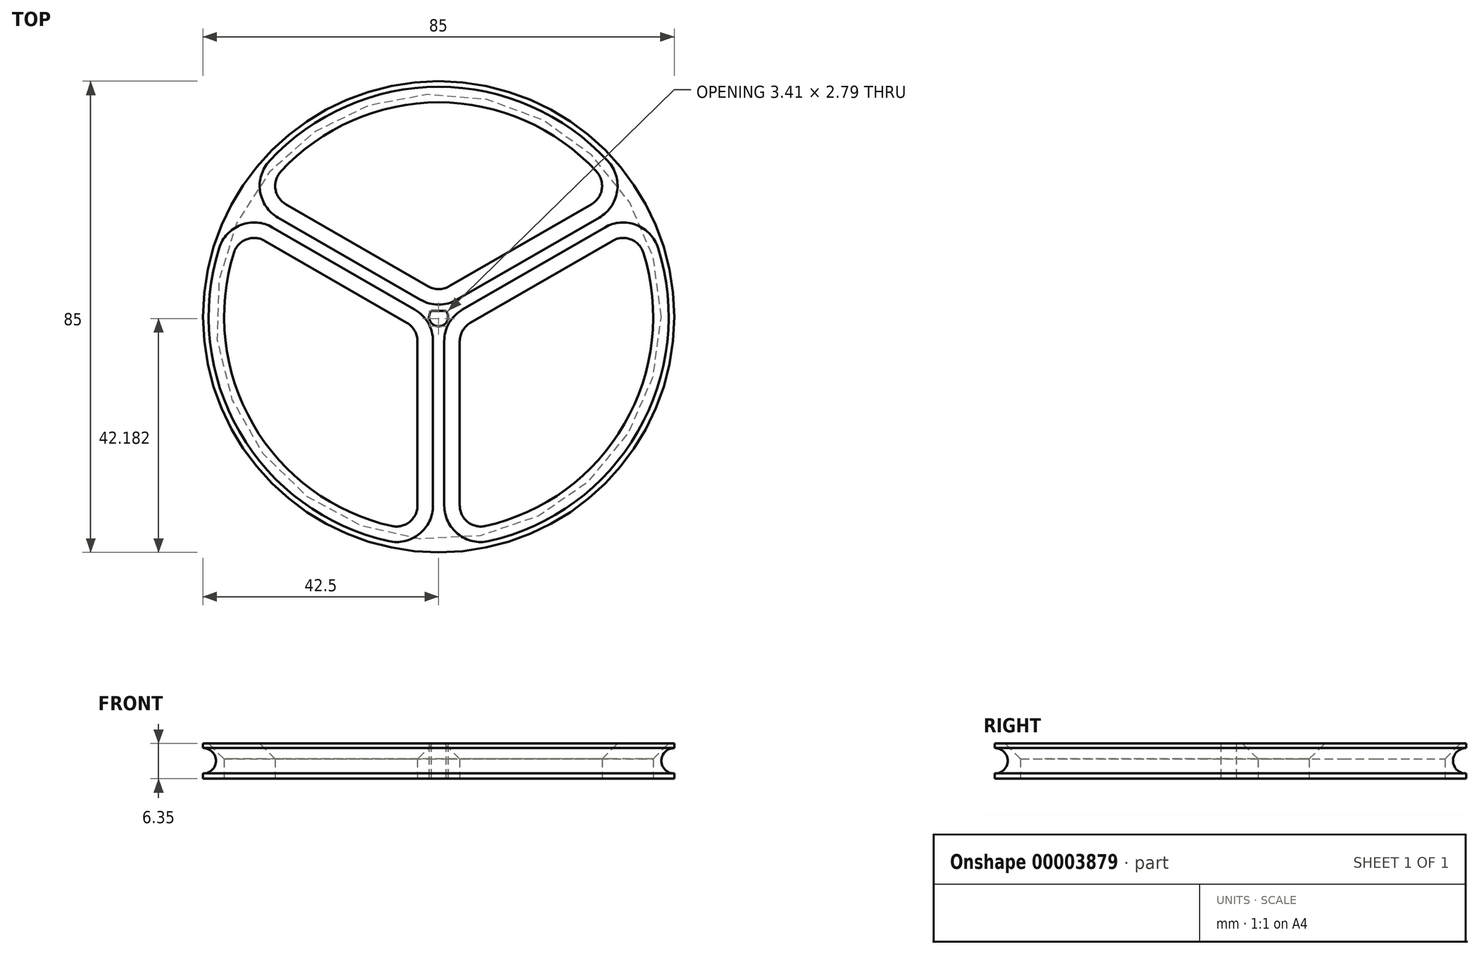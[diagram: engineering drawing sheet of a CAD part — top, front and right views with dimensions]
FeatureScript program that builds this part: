
annotation { "Feature Type Name" : "Feature", "Feature Type Description" : "" }
export const myFeature = defineFeature(function(context is Context, id is Id, definition is map)
    precondition{}
    {
        {
            var Q0;
            Q0=qCreatedBy(makeId("Top.planeOp"),FACE);
            var sketch = newSketch(context, id + "F0", { "sketchPlane" : qUnion([Q0])});
            skCircle(sketch, "E0", {"center": v(0, 0) * mm, "radius": 42.5 * mm});
            skLineSegment(sketch, "E1", {"start": v(0, 0) * mm, "end": v(-36.8, 21.25) * mm});
            skLineSegment(sketch, "E2", {"start": v(0, 0) * mm, "end": v(36.8, 21.25) * mm});
            skLineSegment(sketch, "E3", {"start": v(0, 0) * mm, "end": v(-36.8, -21.25) * mm, "construction": true});
            skLineSegment(sketch, "E4", {"start": v(0, 0) * mm, "end": v(0, -42.5) * mm});
            skLineSegment(sketch, "E5", {"start": v(0, 0) * mm, "end": v(36.8, -21.25) * mm, "construction": true});
            skLineSegment(sketch, "E6", {"start": v(0, 0) * mm, "end": v(0, 42.5) * mm, "construction": true});
            skArc(sketch, "E7", {"start": v(-1.33, 1.08) * mm, "mid": v(0, -1.71) * mm, "end": v(1.33, 1.08) * mm});
            skPoint(sketch, "E8", {"position": v(0, 1.08) * mm});
            skLineSegment(sketch, "E9", {"start": v(0, 1.08) * mm, "end": v(1.33, 1.08) * mm});
            skLineSegment(sketch, "E10", {"start": v(0, 1.08) * mm, "end": v(-1.33, 1.08) * mm});
            skLineSegment(sketch, "E11.0", {"start": v(5.71, -1.1) * mm, "end": v(31.38, 13.72) * mm});
            skLineSegment(sketch, "E11.1", {"start": v(3.81, -4.4) * mm, "end": v(3.81, -34.04) * mm});
            skLineSegment(sketch, "E12.0", {"start": v(-5.71, -1.1) * mm, "end": v(-31.38, 13.72) * mm});
            skLineSegment(sketch, "E12.1", {"start": v(-3.81, -4.4) * mm, "end": v(-3.8, -34.04) * mm});
            skLineSegment(sketch, "E13.0", {"start": v(-1.9, 5.5) * mm, "end": v(-27.57, 20.32) * mm});
            skLineSegment(sketch, "E13.1", {"start": v(1.9, 5.5) * mm, "end": v(27.57, 20.32) * mm});
            skArc(sketch, "E14", {"start": v(-36.92, 11.56) * mm, "mid": v(-33.5, -19.35) * mm, "end": v(-8.45, -37.76) * mm});
            skArc(sketch, "E15", {"start": v(8.45, -37.76) * mm, "mid": v(33.5, -19.35) * mm, "end": v(36.92, 11.56) * mm});
            skArc(sketch, "E16", {"start": v(28.47, 26.2) * mm, "mid": v(0, 38.7) * mm, "end": v(-28.47, 26.2) * mm});
            skPoint(sketch, "E17.visualSharp", {"position": v(-31.44, 22.55) * mm});
            skArc(sketch, "E17.filletArc", {"start": v(-28.47, 26.2) * mm, "mid": v(-29.43, 23.04) * mm, "end": v(-27.57, 20.32) * mm});
            skPoint(sketch, "E18.visualSharp", {"position": v(31.44, 22.55) * mm});
            skArc(sketch, "E18.filletArc", {"start": v(27.57, 20.32) * mm, "mid": v(29.43, 23.04) * mm, "end": v(28.47, 26.2) * mm});
            skPoint(sketch, "E19.visualSharp", {"position": v(0, 4.4) * mm});
            skArc(sketch, "E19.filletArc", {"start": v(-1.9, 5.5) * mm, "mid": v(0, 4.99) * mm, "end": v(1.9, 5.5) * mm});
            skPoint(sketch, "E20.visualSharp", {"position": v(-3.8, -2.2) * mm});
            skArc(sketch, "E20.filletArc", {"start": v(-3.81, -4.4) * mm, "mid": v(-4.32, -2.5) * mm, "end": v(-5.71, -1.1) * mm});
            skPoint(sketch, "E21.visualSharp", {"position": v(-35.25, 15.95) * mm});
            skArc(sketch, "E21.filletArc", {"start": v(-31.38, 13.72) * mm, "mid": v(-34.67, 13.97) * mm, "end": v(-36.92, 11.56) * mm});
            skPoint(sketch, "E22.visualSharp", {"position": v(-3.8, -38.5) * mm});
            skArc(sketch, "E22.filletArc", {"start": v(-8.45, -37.76) * mm, "mid": v(-5.24, -37.01) * mm, "end": v(-3.8, -34.04) * mm});
            skPoint(sketch, "E23.visualSharp", {"position": v(3.81, -38.5) * mm});
            skArc(sketch, "E23.filletArc", {"start": v(3.81, -34.04) * mm, "mid": v(5.24, -37.01) * mm, "end": v(8.45, -37.76) * mm});
            skPoint(sketch, "E24.visualSharp", {"position": v(3.8, -2.2) * mm});
            skArc(sketch, "E24.filletArc", {"start": v(5.71, -1.1) * mm, "mid": v(4.32, -2.5) * mm, "end": v(3.8, -4.4) * mm});
            skPoint(sketch, "E25.visualSharp", {"position": v(35.25, 15.95) * mm});
            skArc(sketch, "E25.filletArc", {"start": v(36.92, 11.56) * mm, "mid": v(34.67, 13.97) * mm, "end": v(31.38, 13.72) * mm});
            skSolve(sketch);
        }
        {
            var Q0;
            {var subQ1=sQuery(id+"F0.wireOp",EDGE,"E9");Q0=qUnion([makeQuery(id+"F0.imprint","IMPRINT",FACE,{"disambiguationData":[TD([[makeQuery(id+"F0.imprint","IMPRINT",EDGE,{"derivedFrom":subQ1}),1.0]])]}),makeQuery(id+"F0.imprint","IMPRINT",FACE,{"disambiguationData":[TD([[makeQuery(id+"F0.imprint","IMPRINT",EDGE,{"derivedFrom":sQuery(id+"F0.wireOp",EDGE,"E12.0")}),-1.0]])]}),makeQuery(id+"F0.imprint","IMPRINT",FACE,{"disambiguationData":[TD([[makeQuery(id+"F0.imprint","IMPRINT",EDGE,{"derivedFrom":sQuery(id+"F0.wireOp",EDGE,"E11.0")}),1.0]])]})]);}
            extrude(context, id + "F1", {"entities" : qUnion([Q0]), "depth" : 6.35 * mm});
        }
        {
            var Q0;
            Q0=makeQuery(id+"F1.opExtrude","CAP_EDGE",EDGE,{"disambiguationData":[OSD([sQuery(id+"F0.wireOp",EDGE,"E16")])],"isStart":false});
            var Q1;
            Q1=makeQuery(id+"F1.opExtrude","CAP_EDGE",EDGE,{"disambiguationData":[OSD([sQuery(id+"F0.wireOp",EDGE,"E17.filletArc")])],"isStart":false});
            var Q2;
            Q2=makeQuery(id+"F1.opExtrude","CAP_EDGE",EDGE,{"disambiguationData":[OSD([sQuery(id+"F0.wireOp",EDGE,"E13.0")])],"isStart":false});
            var Q3;
            Q3=makeQuery(id+"F1.opExtrude","CAP_EDGE",EDGE,{"disambiguationData":[OSD([sQuery(id+"F0.wireOp",EDGE,"E19.filletArc")])],"isStart":false});
            var Q4;
            Q4=makeQuery(id+"F1.opExtrude","CAP_EDGE",EDGE,{"disambiguationData":[OSD([sQuery(id+"F0.wireOp",EDGE,"E13.1")])],"isStart":false});
            var Q5;
            Q5=makeQuery(id+"F1.opExtrude","CAP_EDGE",EDGE,{"disambiguationData":[OSD([sQuery(id+"F0.wireOp",EDGE,"E18.filletArc")])],"isStart":false});
            var Q6;
            Q6=makeQuery(id+"F1.opExtrude","CAP_EDGE",EDGE,{"disambiguationData":[OSD([sQuery(id+"F0.wireOp",EDGE,"E12.0")])],"isStart":false});
            var Q7;
            Q7=makeQuery(id+"F1.opExtrude","CAP_EDGE",EDGE,{"disambiguationData":[OSD([sQuery(id+"F0.wireOp",EDGE,"E21.filletArc")])],"isStart":false});
            var Q8;
            Q8=makeQuery(id+"F1.opExtrude","CAP_EDGE",EDGE,{"disambiguationData":[OSD([sQuery(id+"F0.wireOp",EDGE,"E14")])],"isStart":false});
            var Q9;
            Q9=makeQuery(id+"F1.opExtrude","CAP_EDGE",EDGE,{"disambiguationData":[OSD([sQuery(id+"F0.wireOp",EDGE,"E22.filletArc")])],"isStart":false});
            var Q10;
            Q10=makeQuery(id+"F1.opExtrude","CAP_EDGE",EDGE,{"disambiguationData":[OSD([sQuery(id+"F0.wireOp",EDGE,"E12.1")])],"isStart":false});
            var Q11;
            Q11=makeQuery(id+"F1.opExtrude","CAP_EDGE",EDGE,{"disambiguationData":[OSD([sQuery(id+"F0.wireOp",EDGE,"E20.filletArc")])],"isStart":false});
            var Q12;
            Q12=makeQuery(id+"F1.opExtrude","CAP_EDGE",EDGE,{"disambiguationData":[OSD([sQuery(id+"F0.wireOp",EDGE,"E11.1")])],"isStart":false});
            var Q13;
            Q13=makeQuery(id+"F1.opExtrude","CAP_EDGE",EDGE,{"disambiguationData":[OSD([sQuery(id+"F0.wireOp",EDGE,"E24.filletArc")])],"isStart":false});
            var Q14;
            Q14=makeQuery(id+"F1.opExtrude","CAP_EDGE",EDGE,{"disambiguationData":[OSD([sQuery(id+"F0.wireOp",EDGE,"E11.0")])],"isStart":false});
            var Q15;
            Q15=makeQuery(id+"F1.opExtrude","CAP_EDGE",EDGE,{"disambiguationData":[OSD([sQuery(id+"F0.wireOp",EDGE,"E25.filletArc")])],"isStart":false});
            var Q16;
            Q16=makeQuery(id+"F1.opExtrude","CAP_EDGE",EDGE,{"disambiguationData":[OSD([sQuery(id+"F0.wireOp",EDGE,"E15")])],"isStart":false});
            var Q17;
            Q17=makeQuery(id+"F1.opExtrude","CAP_EDGE",EDGE,{"disambiguationData":[OSD([sQuery(id+"F0.wireOp",EDGE,"E23.filletArc")])],"isStart":false});
            chamfer(context, id + "F2", {"entities" : qUnion([Q0, Q1, Q2, Q3, Q4, Q5, Q6, Q7, Q8, Q9, Q10, Q11, Q12, Q13, Q14, Q15, Q16, Q17]), "width" : 2.8 * mm, "tangentPropagation" : true});
        }
        {
            var Q0;
            Q0=qCreatedBy(makeId("Front.planeOp"),FACE);
            var sketch = newSketch(context, id + "F3", { "sketchPlane" : qUnion([Q0])});
            skCircle(sketch, "E26", {"center": v(-42.45, 3.24) * mm, "radius": 2.29 * mm});
            skLineSegment(sketch, "E27", {"start": v(0, 0) * mm, "end": v(0, 16.32) * mm, "construction": true});
            skSolve(sketch);
        }
        {
            var Q0;
            Q0=makeQuery(id+"F3.imprint","IMPRINT",FACE,{"disambiguationData":[TD([[makeQuery(id+"F3.imprint","IMPRINT",EDGE,{"derivedFrom":sQuery(id+"F3.wireOp",EDGE,"E26")}),1.0]])]});
            var Q1;
            Q1=sQuery(id+"F3.wireOp",EDGE,"E26");
            var Q2;
            Q2=sQuery(id+"F3.wireOp",EDGE,"E27");
            revolve(context, id + "F4", {"operationType" : NewBodyOperationType.REMOVE, "entities" : qUnion([Q0]), "surfaceEntities" : qUnion([Q1]), "axis" : qUnion([Q2]), "revolveType" : RevolveType.FULL, "oppositeDirection" : true});
        }
    });
